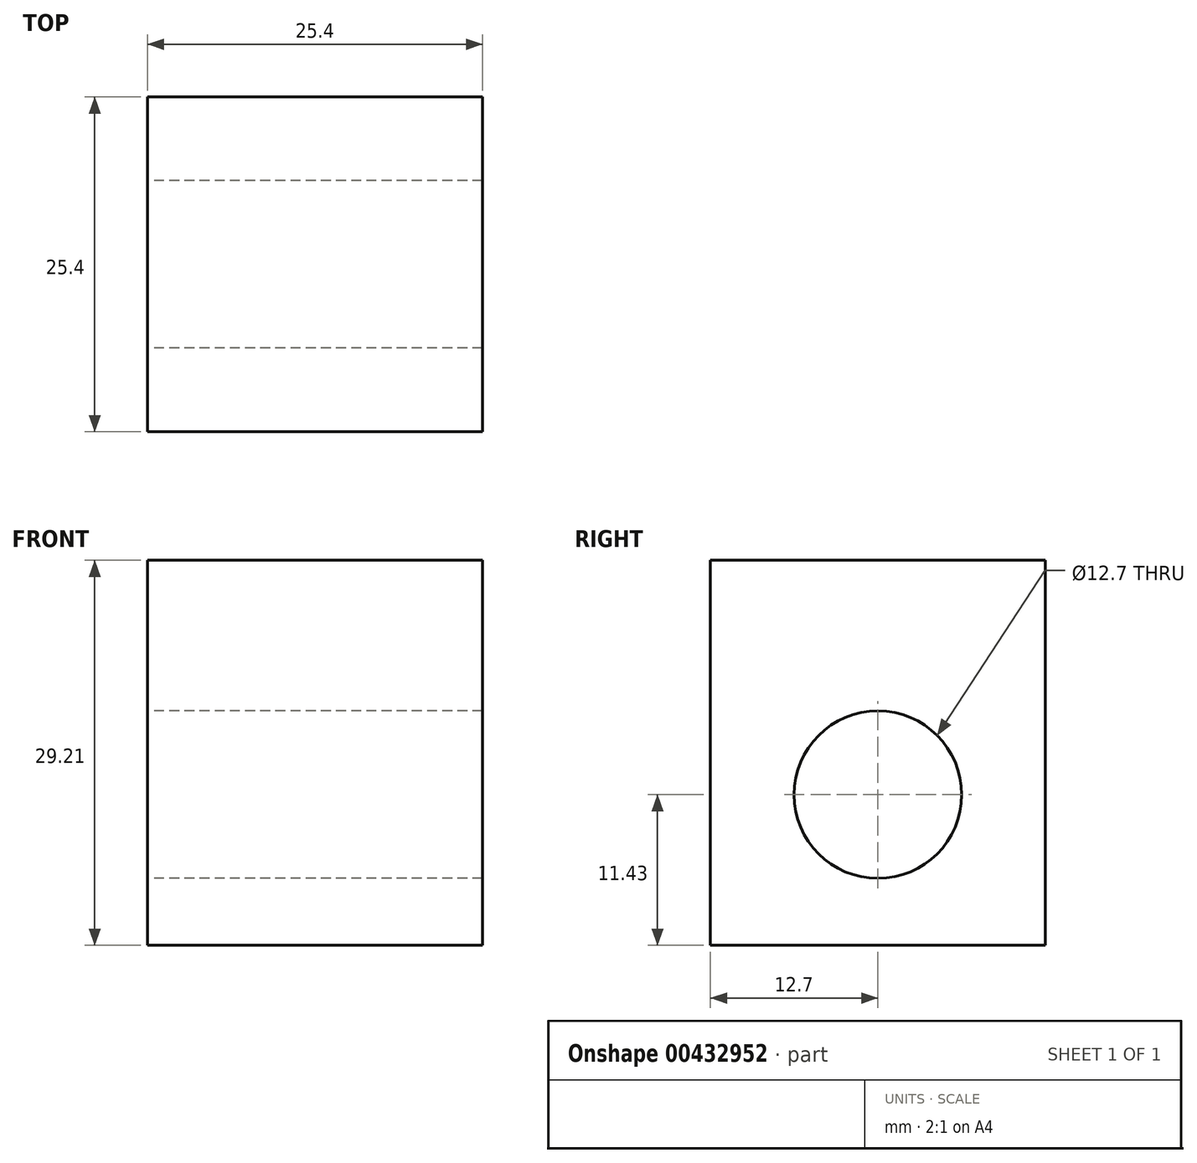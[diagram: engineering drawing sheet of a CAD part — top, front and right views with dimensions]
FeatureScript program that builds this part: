
annotation { "Feature Type Name" : "Feature", "Feature Type Description" : "" }
export const myFeature = defineFeature(function(context is Context, id is Id, definition is map)
    precondition{}
    {
        {
            var Q0;
            Q0=qCreatedBy(makeId("Right.planeOp"),FACE);
            var sketch = newSketch(context, id + "F0", { "sketchPlane" : qUnion([Q0])});
            skLineSegment(sketch, "E0.bottom", {"start": v(12.7, -6.35) * mm, "end": v(-12.7, -6.35) * mm});
            skLineSegment(sketch, "E0.top", {"start": v(12.7, 6.35) * mm, "end": v(-12.7, 6.35) * mm});
            skLineSegment(sketch, "E0.left", {"start": v(12.7, -6.35) * mm, "end": v(12.7, 6.35) * mm});
            skLineSegment(sketch, "E0.right", {"start": v(-12.7, -6.35) * mm, "end": v(-12.7, 6.35) * mm});
            skPoint(sketch, "E0.middle", {"position": v(0, 0) * mm});
            skCircle(sketch, "E1", {"center": v(0, -11.43) * mm, "radius": 6.35 * mm});
            skPoint(sketch, "E1.centerSnap0", {"position": v(0, -6.35) * mm});
            skLineSegment(sketch, "E2", {"start": v(12.7, -6.35) * mm, "end": v(12.7, -22.86) * mm});
            skLineSegment(sketch, "E3.MirrorCS", {"start": v(-12.7, -6.35) * mm, "end": v(-12.7, -22.86) * mm});
            skLineSegment(sketch, "E4", {"start": v(-12.7, -22.86) * mm, "end": v(12.7, -22.86) * mm});
            skSolve(sketch);
        }
        {
            var Q0;
            Q0=makeQuery(id+"F0.imprint","IMPRINT",FACE,{"disambiguationData":[TD([[makeQuery(id+"F0.imprint","IMPRINT",EDGE,{"derivedFrom":sQuery(id+"F0.wireOp",EDGE,"E0.top")}),1.0]])]});
            var Q1;
            {var subQ0=sQuery(id+"F0.wireOp",EDGE,"E2");Q1=makeQuery(id+"F0.imprint","IMPRINT",FACE,{"disambiguationData":[TD([[makeQuery(id+"F0.imprint","IMPRINT",EDGE,{"derivedFrom":subQ0}),-1.0]])]});}
            extrude(context, id + "F1", {"entities" : qUnion([Q0, Q1]), "depth" : 25.4 * mm});
        }
    });
